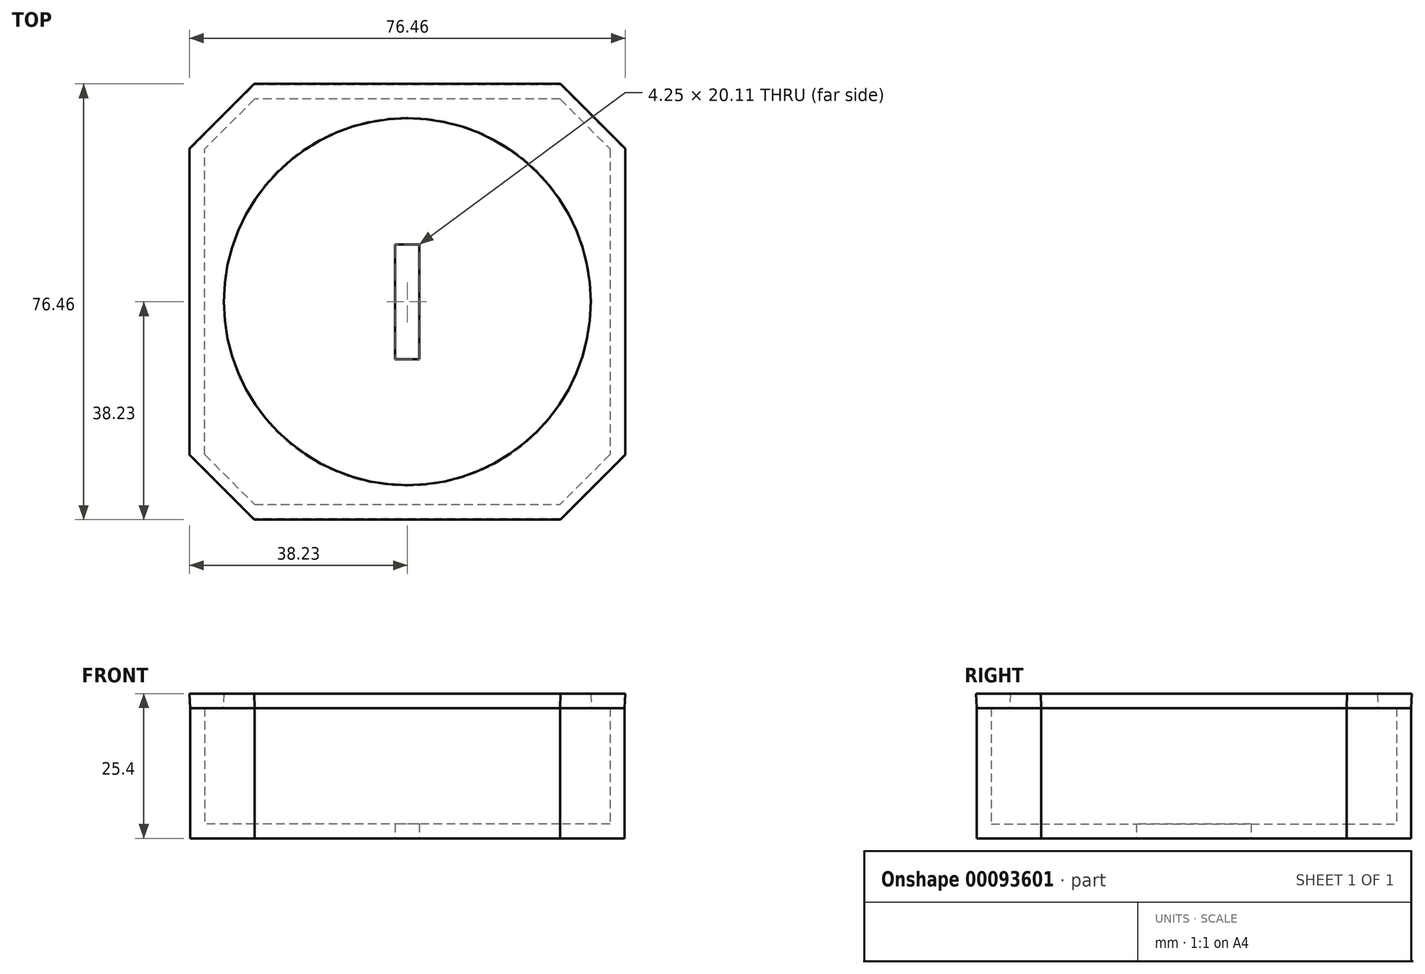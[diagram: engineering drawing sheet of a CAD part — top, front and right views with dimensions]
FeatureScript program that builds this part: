
annotation { "Feature Type Name" : "Feature", "Feature Type Description" : "" }
export const myFeature = defineFeature(function(context is Context, id is Id, definition is map)
    precondition{}
    {
        {
            var Q0;
            Q0=qCreatedBy(makeId("Top.planeOp"),FACE);
            var sketch = newSketch(context, id + "F0", { "sketchPlane" : qUnion([Q0])});
            skPoint(sketch, "E0", {"position": v(0, 0) * mm});
            skLineSegment(sketch, "E1.bottom", {"start": v(26.8, 38.1) * mm, "end": v(-26.8, 38.1) * mm});
            skLineSegment(sketch, "E1.top", {"start": v(26.8, -38.1) * mm, "end": v(-26.8, -38.1) * mm});
            skLineSegment(sketch, "E1.left", {"start": v(26.8, 38.1) * mm, "end": v(26.8, -38.1) * mm});
            skLineSegment(sketch, "E1.right", {"start": v(-26.8, 38.1) * mm, "end": v(-26.8, -38.1) * mm});
            skLineSegment(sketch, "E2.bottom", {"start": v(38.1, 26.8) * mm, "end": v(-38.1, 26.8) * mm});
            skLineSegment(sketch, "E2.top", {"start": v(38.1, -26.8) * mm, "end": v(-38.1, -26.8) * mm});
            skLineSegment(sketch, "E2.left", {"start": v(38.1, 26.8) * mm, "end": v(38.1, -26.8) * mm});
            skLineSegment(sketch, "E2.right", {"start": v(-38.1, 26.8) * mm, "end": v(-38.1, -26.8) * mm});
            skPoint(sketch, "E3", {"position": v(-26.8, -38.1) * mm});
            skPoint(sketch, "E4", {"position": v(-26.8, 38.1) * mm});
            skPoint(sketch, "E5", {"position": v(26.8, 38.1) * mm});
            skPoint(sketch, "E6", {"position": v(26.8, -38.1) * mm});
            skPoint(sketch, "E7", {"position": v(38.1, -26.8) * mm});
            skPoint(sketch, "E8", {"position": v(38.1, 26.8) * mm});
            skPoint(sketch, "E9", {"position": v(-38.1, 26.8) * mm});
            skPoint(sketch, "E10", {"position": v(-38.1, -26.8) * mm});
            skLineSegment(sketch, "E11", {"start": v(26.8, 38.1) * mm, "end": v(38.1, 26.8) * mm});
            skLineSegment(sketch, "E12", {"start": v(26.8, -38.1) * mm, "end": v(38.1, -26.8) * mm});
            skLineSegment(sketch, "E13", {"start": v(-38.1, -26.8) * mm, "end": v(-26.8, -38.1) * mm});
            skLineSegment(sketch, "E14", {"start": v(-38.1, 26.8) * mm, "end": v(-26.8, 38.1) * mm});
            skPoint(sketch, "E15", {"position": v(-26.8, 35.56) * mm});
            skPoint(sketch, "E16", {"position": v(-35.56, 26.8) * mm});
            skPoint(sketch, "E17", {"position": v(-26.8, -35.56) * mm});
            skPoint(sketch, "E18", {"position": v(-35.56, -26.8) * mm});
            skPoint(sketch, "E19", {"position": v(26.8, -35.56) * mm});
            skPoint(sketch, "E20", {"position": v(35.56, -26.8) * mm});
            skPoint(sketch, "E21", {"position": v(35.56, 26.8) * mm});
            skPoint(sketch, "E22", {"position": v(26.8, 35.56) * mm});
            skLineSegment(sketch, "E23", {"start": v(-26.8, -35.56) * mm, "end": v(-35.56, -26.8) * mm});
            skLineSegment(sketch, "E24", {"start": v(-35.56, 26.8) * mm, "end": v(-26.8, 35.56) * mm});
            skLineSegment(sketch, "E25", {"start": v(35.56, 26.8) * mm, "end": v(26.8, 35.56) * mm});
            skLineSegment(sketch, "E26", {"start": v(26.8, -35.56) * mm, "end": v(35.56, -26.8) * mm});
            skLineSegment(sketch, "E27", {"start": v(26.8, -35.56) * mm, "end": v(-26.8, -35.56) * mm});
            skLineSegment(sketch, "E28", {"start": v(35.56, -26.8) * mm, "end": v(35.56, 26.8) * mm});
            skLineSegment(sketch, "E29", {"start": v(-35.56, 26.8) * mm, "end": v(-35.56, -26.8) * mm});
            skLineSegment(sketch, "E30", {"start": v(-26.8, 35.56) * mm, "end": v(26.8, 35.56) * mm});
            skSolve(sketch);
        }
        {
            var Q0;
            Q0=qCreatedBy(makeId("Top.planeOp"),FACE);
            cPlane(context, id + "F1", {"entities" : qUnion([Q0]), "cplaneType" : CPlaneType.OFFSET, "offset" : 22.86 * mm, "width" : 152.4 * mm, "height" : 152.4 * mm});
        }
        {
            var Q0;
            Q0=qCreatedBy(id+"F1.planeOp",FACE);
            var sketch = newSketch(context, id + "F5", { "sketchPlane" : qUnion([Q0])});
            skPoint(sketch, "E31", {"position": v(0, 0) * mm});
            skLineSegment(sketch, "E32.bottom", {"start": v(26.8, 38.1) * mm, "end": v(-26.8, 38.1) * mm});
            skLineSegment(sketch, "E32.top", {"start": v(26.8, -38.1) * mm, "end": v(-26.8, -38.1) * mm});
            skLineSegment(sketch, "E32.left", {"start": v(26.8, 38.1) * mm, "end": v(26.8, -38.1) * mm});
            skLineSegment(sketch, "E32.right", {"start": v(-26.8, 38.1) * mm, "end": v(-26.8, -38.1) * mm});
            skLineSegment(sketch, "E33.bottom", {"start": v(38.1, 26.8) * mm, "end": v(-38.1, 26.8) * mm});
            skLineSegment(sketch, "E33.top", {"start": v(38.1, -26.8) * mm, "end": v(-38.1, -26.8) * mm});
            skLineSegment(sketch, "E33.left", {"start": v(38.1, 26.8) * mm, "end": v(38.1, -26.8) * mm});
            skLineSegment(sketch, "E33.right", {"start": v(-38.1, 26.8) * mm, "end": v(-38.1, -26.8) * mm});
            skPoint(sketch, "E34", {"position": v(-38.1, 26.8) * mm});
            skPoint(sketch, "E35", {"position": v(-26.8, 38.1) * mm});
            skPoint(sketch, "E36", {"position": v(26.8, 38.1) * mm});
            skPoint(sketch, "E37", {"position": v(38.1, 26.8) * mm});
            skPoint(sketch, "E38", {"position": v(38.1, -26.8) * mm});
            skPoint(sketch, "E39", {"position": v(26.8, -38.1) * mm});
            skPoint(sketch, "E40", {"position": v(-26.8, -38.1) * mm});
            skPoint(sketch, "E41", {"position": v(-38.1, -26.8) * mm});
            skCircle(sketch, "E42", {"center": v(0, 0) * mm, "radius": 32.31 * mm});
            skLineSegment(sketch, "E43", {"start": v(26.8, -38.1) * mm, "end": v(38.1, -26.8) * mm});
            skLineSegment(sketch, "E44", {"start": v(-26.8, -38.1) * mm, "end": v(-38.1, -26.8) * mm});
            skLineSegment(sketch, "E45", {"start": v(38.1, 26.8) * mm, "end": v(26.8, 38.1) * mm});
            skLineSegment(sketch, "E46", {"start": v(-38.1, 26.8) * mm, "end": v(-26.8, 38.1) * mm});
            skSolve(sketch);
        }
        {
            var Q0;
            {var subQ0=sQuery(id+"F0.wireOp",EDGE,"E2.bottom");var subQ1=sQuery(id+"F0.wireOp",EDGE,"E1.left");var subQ2=makeQuery(id+"F0.imprint","INTERSECT",VERTEX,{"derivedFrom":[subQ1,subQ0]});Q0=makeQuery(id+"F0.imprint","IMPRINT",FACE,{"disambiguationData":[TD([[makeQuery(id+"F0.imprint","IMPRINT",EDGE,{"disambiguationData":[TD([[subQ2,-1.0]])],"derivedFrom":subQ1}),-1.0]])]});}
            var sketch = newSketch(context, id + "F2", { "sketchPlane" : qUnion([Q0])});
            skLineSegment(sketch, "E47.bottom", {"start": v(2.12, 10.06) * mm, "end": v(-2.12, 10.06) * mm});
            skLineSegment(sketch, "E47.top", {"start": v(2.12, -10.06) * mm, "end": v(-2.12, -10.06) * mm});
            skLineSegment(sketch, "E47.left", {"start": v(2.12, 10.06) * mm, "end": v(2.12, -10.06) * mm});
            skLineSegment(sketch, "E47.right", {"start": v(-2.12, 10.06) * mm, "end": v(-2.12, -10.06) * mm});
            skPoint(sketch, "E47.middle", {"position": v(0, 0) * mm});
            skSolve(sketch);
        }
        {
            var Q0;
            {var subQ0=sQuery(id+"F5.wireOp",EDGE,"E44");Q0=makeQuery(id+"F5.imprint","IMPRINT",FACE,{"disambiguationData":[TD([[makeQuery(id+"F5.imprint","IMPRINT",EDGE,{"derivedFrom":subQ0}),-1.0]])]});}
            var Q1;
            {var subQ0=sQuery(id+"F5.wireOp",EDGE,"E42");var subQ1=sQuery(id+"F5.wireOp",EDGE,"E32.right");var subQ2=makeQuery(id+"F5.imprint","INTERSECT",VERTEX,{"disambiguationData":[OD(1.0)],"derivedFrom":[subQ1,subQ0]});Q1=makeQuery(id+"F5.imprint","IMPRINT",FACE,{"disambiguationData":[TD([[makeQuery(id+"F5.imprint","IMPRINT",EDGE,{"disambiguationData":[TD([[subQ2,-1.0]])],"derivedFrom":subQ1}),1.0]])]});}
            var Q2;
            {var subQ0=sQuery(id+"F5.wireOp",EDGE,"E45");Q2=makeQuery(id+"F5.imprint","IMPRINT",FACE,{"disambiguationData":[TD([[makeQuery(id+"F5.imprint","IMPRINT",EDGE,{"derivedFrom":subQ0}),1.0]])]});}
            var Q3;
            {var subQ0=sQuery(id+"F5.wireOp",EDGE,"E33.bottom");var subQ1=sQuery(id+"F5.wireOp",EDGE,"E32.left");var subQ2=makeQuery(id+"F5.imprint","INTERSECT",VERTEX,{"derivedFrom":[subQ1,subQ0]});Q3=makeQuery(id+"F5.imprint","IMPRINT",FACE,{"disambiguationData":[TD([[makeQuery(id+"F5.imprint","IMPRINT",EDGE,{"disambiguationData":[TD([[subQ2,-1.0]])],"derivedFrom":subQ1}),-1.0]])]});}
            var Q4;
            {var subQ0=sQuery(id+"F5.wireOp",EDGE,"E33.bottom");var subQ1=sQuery(id+"F5.wireOp",EDGE,"E32.right");var subQ2=makeQuery(id+"F5.imprint","INTERSECT",VERTEX,{"derivedFrom":[subQ1,subQ0]});Q4=makeQuery(id+"F5.imprint","IMPRINT",FACE,{"disambiguationData":[TD([[makeQuery(id+"F5.imprint","IMPRINT",EDGE,{"disambiguationData":[TD([[subQ2,-1.0]])],"derivedFrom":subQ1}),1.0]])]});}
            var Q5;
            {var subQ0=sQuery(id+"F5.wireOp",EDGE,"E43");Q5=makeQuery(id+"F5.imprint","IMPRINT",FACE,{"disambiguationData":[TD([[makeQuery(id+"F5.imprint","IMPRINT",EDGE,{"derivedFrom":subQ0}),1.0]])]});}
            var Q6;
            {var subQ0=sQuery(id+"F5.wireOp",EDGE,"E33.left");Q6=makeQuery(id+"F5.imprint","IMPRINT",FACE,{"disambiguationData":[TD([[makeQuery(id+"F5.imprint","IMPRINT",EDGE,{"derivedFrom":subQ0}),-1.0]])]});}
            var Q7;
            {var subQ1=sQuery(id+"F5.wireOp",EDGE,"E32.top");Q7=makeQuery(id+"F5.imprint","IMPRINT",FACE,{"disambiguationData":[TD([[makeQuery(id+"F5.imprint","IMPRINT",EDGE,{"derivedFrom":subQ1}),-1.0]])]});}
            var Q8;
            {var subQ0=sQuery(id+"F5.wireOp",EDGE,"E46");Q8=makeQuery(id+"F5.imprint","IMPRINT",FACE,{"disambiguationData":[TD([[makeQuery(id+"F5.imprint","IMPRINT",EDGE,{"derivedFrom":subQ0}),-1.0]])]});}
            var Q9;
            {var subQ6=sQuery(id+"F5.wireOp",EDGE,"E32.bottom");Q9=makeQuery(id+"F5.imprint","IMPRINT",FACE,{"disambiguationData":[TD([[makeQuery(id+"F5.imprint","IMPRINT",EDGE,{"derivedFrom":subQ6}),1.0]])]});}
            var Q10;
            {var subQ0=sQuery(id+"F5.wireOp",EDGE,"E42");var subQ1=sQuery(id+"F5.wireOp",EDGE,"E32.left");var subQ2=makeQuery(id+"F5.imprint","INTERSECT",VERTEX,{"disambiguationData":[OD(1.0)],"derivedFrom":[subQ1,subQ0]});Q10=makeQuery(id+"F5.imprint","IMPRINT",FACE,{"disambiguationData":[TD([[makeQuery(id+"F5.imprint","IMPRINT",EDGE,{"disambiguationData":[TD([[subQ2,-1.0]])],"derivedFrom":subQ1}),-1.0]])]});}
            var Q11;
            {var subQ0=sQuery(id+"F5.wireOp",EDGE,"E33.right");Q11=makeQuery(id+"F5.imprint","IMPRINT",FACE,{"disambiguationData":[TD([[makeQuery(id+"F5.imprint","IMPRINT",EDGE,{"derivedFrom":subQ0}),1.0]])]});}
            extrude(context, id + "F3", {"entities" : qUnion([Q0, Q1, Q2, Q3, Q4, Q5, Q6, Q7, Q8, Q9, Q10, Q11]), "depth" : 2.54 * mm, "hasDraft" : true, "draftAngle" : 3 * degree});
        }
        {
            var Q0;
            {var subQ0=sQuery(id+"F0.wireOp",EDGE,"E2.left");Q0=makeQuery(id+"F0.imprint","IMPRINT",FACE,{"disambiguationData":[TD([[makeQuery(id+"F0.imprint","IMPRINT",EDGE,{"derivedFrom":subQ0}),-1.0]])]});}
            var Q1;
            {var subQ0=sQuery(id+"F0.wireOp",EDGE,"E12");Q1=makeQuery(id+"F0.imprint","IMPRINT",FACE,{"disambiguationData":[TD([[makeQuery(id+"F0.imprint","IMPRINT",EDGE,{"derivedFrom":subQ0}),1.0]])]});}
            var Q2;
            {var subQ0=sQuery(id+"F0.wireOp",EDGE,"E1.top");Q2=makeQuery(id+"F0.imprint","IMPRINT",FACE,{"disambiguationData":[TD([[makeQuery(id+"F0.imprint","IMPRINT",EDGE,{"derivedFrom":subQ0}),-1.0]])]});}
            var Q3;
            {var subQ0=sQuery(id+"F0.wireOp",EDGE,"E13");Q3=makeQuery(id+"F0.imprint","IMPRINT",FACE,{"disambiguationData":[TD([[makeQuery(id+"F0.imprint","IMPRINT",EDGE,{"derivedFrom":subQ0}),1.0]])]});}
            var Q4;
            {var subQ0=sQuery(id+"F0.wireOp",EDGE,"E2.right");Q4=makeQuery(id+"F0.imprint","IMPRINT",FACE,{"disambiguationData":[TD([[makeQuery(id+"F0.imprint","IMPRINT",EDGE,{"derivedFrom":subQ0}),1.0]])]});}
            var Q5;
            {var subQ0=sQuery(id+"F0.wireOp",EDGE,"E14");Q5=makeQuery(id+"F0.imprint","IMPRINT",FACE,{"disambiguationData":[TD([[makeQuery(id+"F0.imprint","IMPRINT",EDGE,{"derivedFrom":subQ0}),-1.0]])]});}
            var Q6;
            {var subQ0=sQuery(id+"F0.wireOp",EDGE,"E1.bottom");Q6=makeQuery(id+"F0.imprint","IMPRINT",FACE,{"disambiguationData":[TD([[makeQuery(id+"F0.imprint","IMPRINT",EDGE,{"derivedFrom":subQ0}),1.0]])]});}
            var Q7;
            {var subQ0=sQuery(id+"F0.wireOp",EDGE,"E11");Q7=makeQuery(id+"F0.imprint","IMPRINT",FACE,{"disambiguationData":[TD([[makeQuery(id+"F0.imprint","IMPRINT",EDGE,{"derivedFrom":subQ0}),-1.0]])]});}
            extrude(context, id + "F4", {"entities" : qUnion([Q0, Q1, Q2, Q3, Q4, Q5, Q6, Q7]), "operationType" : NewBodyOperationType.ADD, "depth" : 25.4 * mm});
        }
        {
            var Q0;
            {var subQ0=sQuery(id+"F0.wireOp",EDGE,"E25");Q0=makeQuery(id+"F0.imprint","IMPRINT",FACE,{"disambiguationData":[TD([[makeQuery(id+"F0.imprint","IMPRINT",EDGE,{"derivedFrom":subQ0}),1.0]])]});}
            var Q1;
            {var subQ0=sQuery(id+"F0.wireOp",EDGE,"E30");Q1=makeQuery(id+"F0.imprint","IMPRINT",FACE,{"disambiguationData":[TD([[makeQuery(id+"F0.imprint","IMPRINT",EDGE,{"derivedFrom":subQ0}),-1.0]])]});}
            var Q2;
            {var subQ5=sQuery(id+"F0.wireOp",EDGE,"E28");Q2=makeQuery(id+"F0.imprint","IMPRINT",FACE,{"disambiguationData":[TD([[makeQuery(id+"F0.imprint","IMPRINT",EDGE,{"derivedFrom":subQ5}),1.0]])]});}
            var Q3;
            Q3=makeQuery(id+"F2.imprint","IMPRINT",FACE,{"disambiguationData":[TD([[makeQuery(id+"F2.imprint","IMPRINT",EDGE,{"derivedFrom":sQuery(id+"F2.wireOp",EDGE,"E47.bottom")}),-1.0]])]});
            var Q4;
            {var subQ0=sQuery(id+"F0.wireOp",EDGE,"E24");Q4=makeQuery(id+"F0.imprint","IMPRINT",FACE,{"disambiguationData":[TD([[makeQuery(id+"F0.imprint","IMPRINT",EDGE,{"derivedFrom":subQ0}),-1.0]])]});}
            var Q5;
            {var subQ5=sQuery(id+"F0.wireOp",EDGE,"E29");Q5=makeQuery(id+"F0.imprint","IMPRINT",FACE,{"disambiguationData":[TD([[makeQuery(id+"F0.imprint","IMPRINT",EDGE,{"derivedFrom":subQ5}),1.0]])]});}
            var Q6;
            {var subQ0=sQuery(id+"F0.wireOp",EDGE,"E23");Q6=makeQuery(id+"F0.imprint","IMPRINT",FACE,{"disambiguationData":[TD([[makeQuery(id+"F0.imprint","IMPRINT",EDGE,{"derivedFrom":subQ0}),-1.0]])]});}
            var Q7;
            {var subQ0=sQuery(id+"F0.wireOp",EDGE,"E27");Q7=makeQuery(id+"F0.imprint","IMPRINT",FACE,{"disambiguationData":[TD([[makeQuery(id+"F0.imprint","IMPRINT",EDGE,{"derivedFrom":subQ0}),-1.0]])]});}
            var Q8;
            {var subQ0=sQuery(id+"F0.wireOp",EDGE,"E26");Q8=makeQuery(id+"F0.imprint","IMPRINT",FACE,{"disambiguationData":[TD([[makeQuery(id+"F0.imprint","IMPRINT",EDGE,{"derivedFrom":subQ0}),1.0]])]});}
            extrude(context, id + "F6", {"entities" : qUnion([Q0, Q1, Q2, Q3, Q4, Q5, Q6, Q7, Q8]), "operationType" : NewBodyOperationType.ADD, "depth" : 2.54 * mm});
        }
    });
